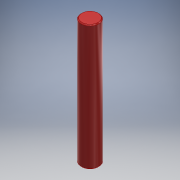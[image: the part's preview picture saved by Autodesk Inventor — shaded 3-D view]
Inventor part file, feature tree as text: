
AUTODESK INVENTOR PART (.ipt)
format: ipt  version: 2018 (Build 220112000, 112)  size: 100,864 bytes
history: native  units: mm
features: extrude x1, chamfer x1, sketch x1
ambient origin geometry x8: Origin, YZ Plane, XZ Plane, XY Plane, X Axis, Y Axis, Z Axis, Center Point
bodies: Solido1 (feature_tree)
feature tree (3):
  extrude  "Estrusione1"  Depth=10.0mm
  chamfer  "Smusso1"  Distance=70.0mm
  sketch  "Schizzo1"
